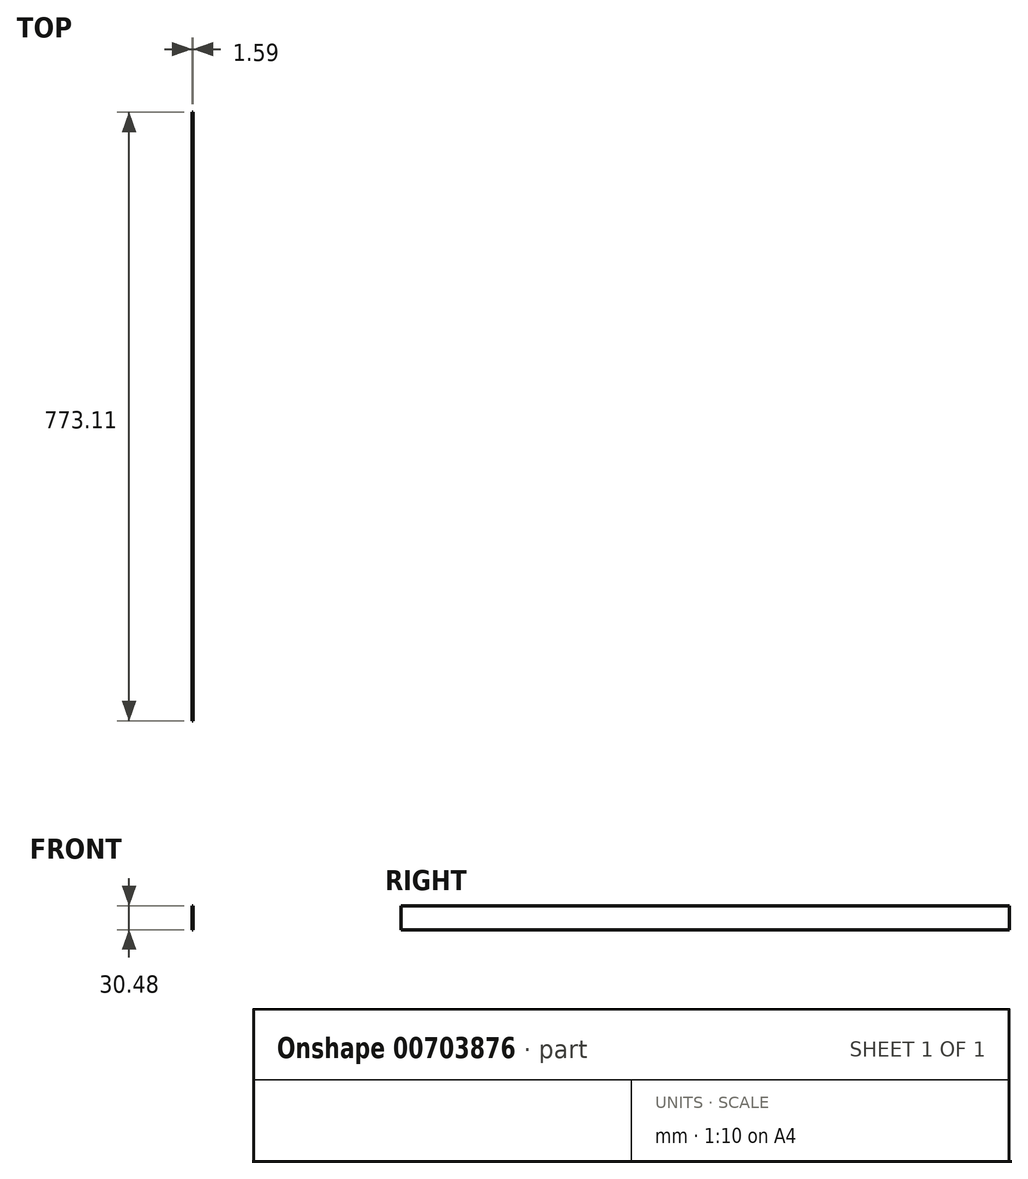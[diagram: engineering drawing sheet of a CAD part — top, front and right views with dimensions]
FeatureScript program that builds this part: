
annotation { "Feature Type Name" : "Feature", "Feature Type Description" : "" }
export const myFeature = defineFeature(function(context is Context, id is Id, definition is map)
    precondition{}
    {
        {
            var Q0;
            Q0=qCreatedBy(makeId("Front.planeOp"),FACE);
            var sketch = newSketch(context, id + "F0", { "sketchPlane" : qUnion([Q0])});
            skLineSegment(sketch, "E0.bottom", {"start": v(0, 0) * mm, "end": v(1.59, 0) * mm});
            skLineSegment(sketch, "E0.top", {"start": v(0, -30.48) * mm, "end": v(1.59, -30.48) * mm});
            skLineSegment(sketch, "E0.left", {"start": v(0, 0) * mm, "end": v(0, -30.48) * mm});
            skLineSegment(sketch, "E0.right", {"start": v(1.59, 0) * mm, "end": v(1.59, -30.48) * mm});
            skSolve(sketch);
        }
        {
            var Q0;
            Q0=qSketchRegion(id+"F0",true);
            extrude(context, id + "F1", {"entities" : qUnion([Q0]), "depth" : 773.1 * mm, "offsetDistance" : 25.4 * mm});
        }
    });
